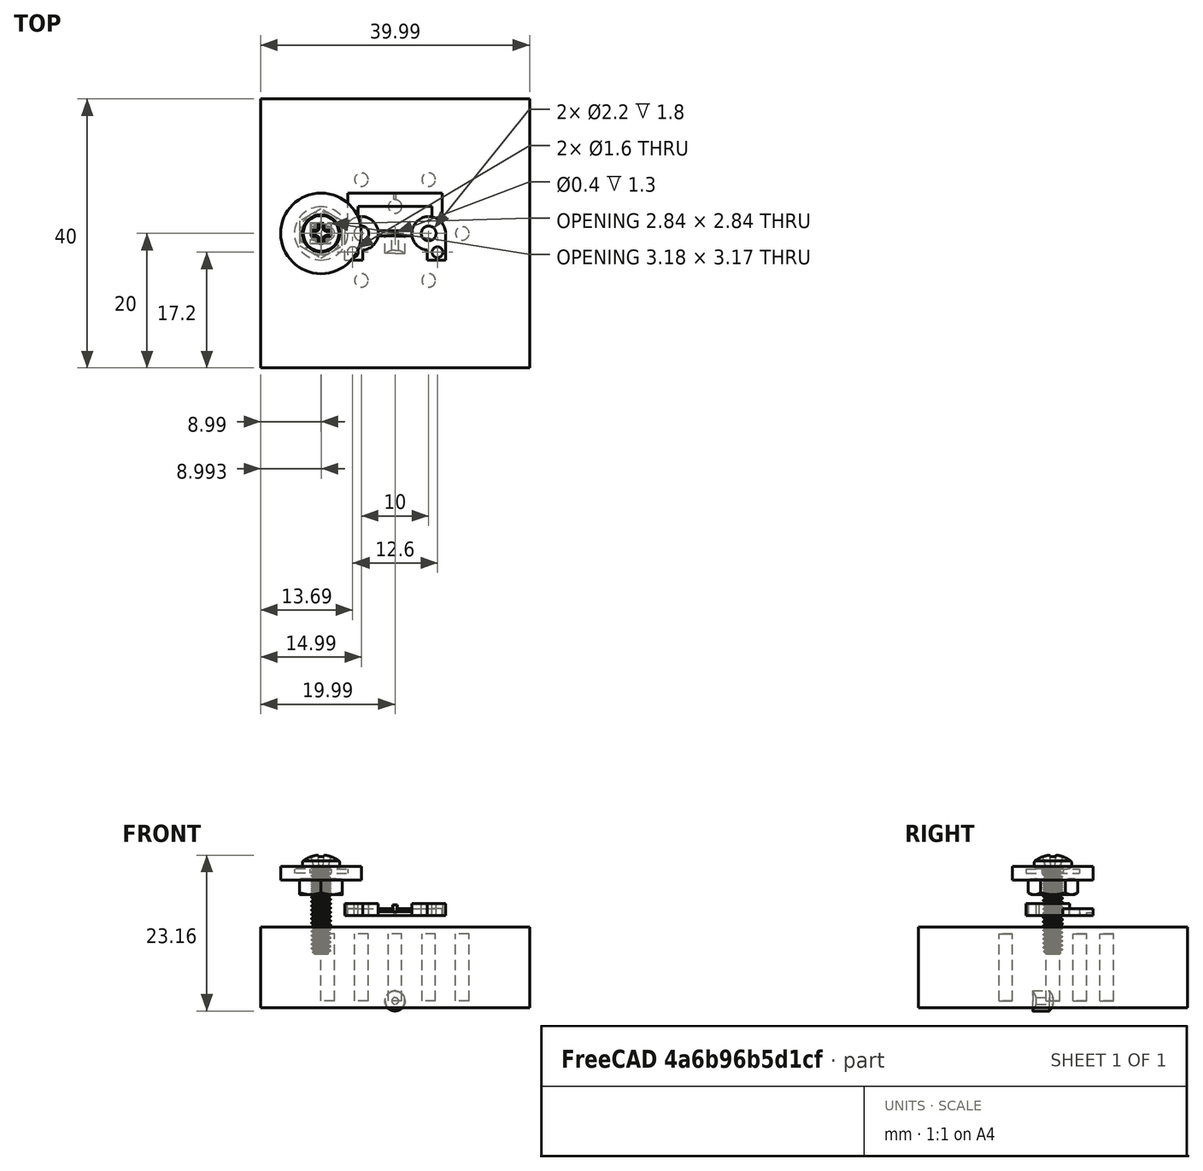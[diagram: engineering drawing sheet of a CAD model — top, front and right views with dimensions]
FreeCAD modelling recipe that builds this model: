
FCSTD DOCUMENT  (FreeCAD 0.18R16033 (Git))
Label: proto_baseplate
License: All rights reserved
LicenseURL: http://en.wikipedia.org/wiki/All_rights_reserved
objects: Part::Cylinder×13, Part::Feature×7, App::Part×4, Path::FeaturePython×4, Part::MultiFuse×3, Part::FeaturePython×2, Part::Cut×1, App::FeaturePython×1, App::DocumentObjectGroup×1, Path::FeatureCompoundPython×1
note: 27 computed .brp shape members not serialized (recipe doc carries the construction recipe); baked Part::Feature solids carry a one-line shape summary decoded from their .brp

FEATURE [Part::Cylinder] Cylinder  label="Baseplate"
  Angle = 360
  AttacherType = Attacher::AttachEngine3D
  Height = 10
  Radius = 19
FEATURE [Part::Cylinder] Cylinder001  label="Recess2"
  Angle = 360
  AttacherType = Attacher::AttachEngine3D
  Height = 1.5
  Placement = pos=(5,0,8.5) rot=(0,0,1;0rad)
  Radius = 1.7
FEATURE [Part::Cylinder] Cylinder002  label="Recess1"
  Angle = 360
  AttacherType = Attacher::AttachEngine3D
  Height = 1.5
  Placement = pos=(-5,0,8.5) rot=(0,0,1;0rad)
  Radius = 1.8
FEATURE [Part::MultiFuse] Fusion004
  Placement = pos=(0,0,13) rot=(0,0,1;0rad)
FEATURE [Part::Feature] Part__Feature  label="1"
  shape: bbox 5.8 x 3 x 3.036 mm, 8 faces (baked)
FEATURE [App::Part] CER_4  label="CER-4"
  Group = -> [Part__Feature]
  Origin = -> Origin
  Placement = pos=(-5,0,13) rot=(1,0,0;1.5708rad)
FEATURE [Part::Feature] Part__Feature001  label="1001"
  shape: bbox 5.8 x 3 x 3.036 mm, 8 faces (baked)
FEATURE [App::Part] CER_005  label="CER-005"
  Group = -> [Part__Feature001]
  Origin = -> Origin001
  Placement = pos=(5,0,13) rot=(1,0,0;1.5708rad)
FEATURE [Part::Feature] Part__Feature002  label="1001001"
  shape: bbox 5.8 x 3 x 3.036 mm, 8 faces (baked)
FEATURE [App::Part] CER_006  label="CER-006"
  Group = -> [Part__Feature002]
  Origin = -> Origin002
  Placement = pos=(5,0,17.5) rot=(1,0,0;1.5708rad)
FEATURE [Part::Feature] Part__Feature003  label="1001001001"
  shape: bbox 5.8 x 3 x 3.036 mm, 8 faces (baked)
FEATURE [App::Part] CER_007  label="CER-007"
  Group = -> [Part__Feature003]
  Origin = -> Origin003
  Placement = pos=(-5,0,17.5) rot=(1,0,0;1.5708rad)
FEATURE [Part::Cylinder] Cylinder003  label="ThreadedHole"
  Angle = 360
  AttacherType = Attacher::AttachEngine3D
  Height = 10
  Placement = pos=(-15,0,0) rot=(0,0,1;0rad)
  Radius = 1
FEATURE [Part::Feature] Part__Feature004  label="90107A005"
  Placement = pos=(-11,0,19) rot=(1,0,0;1.5708rad)
  shape: bbox 7.925 x 7.925 x 0.6096 mm, 6 faces (baked)
FEATURE [Part::Feature] Part__Feature005  label="91772A110"
  Placement = pos=(-11,0,7) rot=(0,0,1;0rad)
  shape: bbox 6.021 x 6.021 x 15.01 mm, 152 faces (baked)
FEATURE [Part::Feature] Part__Feature006  label="91841A005"
  Placement = pos=(-11,0,17) rot=(1,0,0;1.5708rad)
  shape: bbox 7.333 x 7.333 x 2.885 mm, 41 faces (baked)
FEATURE [Part::FeaturePython] Array  # Draft array (typed FeaturePython)
  Angle = 360
  ArrayType = 1
  Axis = (0,0,1)
  Base = -> Cylinder003
  Center = (0,0,0)
  Fuse = false
  IntervalAxis = (0,0,0)
  IntervalX = (1,0,0)
  IntervalY = (0,1,0)
  IntervalZ = (0,0,1)
  NumberPolar = 8
  NumberX = 2
  NumberY = 2
  NumberZ = 1
FEATURE [Part::Cylinder] Cylinder004  label="ThreadedHole001"
  Angle = 360
  AttacherType = Attacher::AttachEngine3D
  Height = 10
  Placement = pos=(0,-4,0) rot=(0,0,1;0rad)
  Radius = 1
FEATURE [Part::MultiFuse] Fusion
  Shapes = -> [Cylinder004,Array,Cylinder002,Cylinder001]
FEATURE [Part::Cut] Cut
  Base = -> Cylinder
  Tool = -> Fusion
FEATURE [App::FeaturePython] SetupSheet  # Path/CAM operation (typed FeaturePython)
  ClearanceHeightExpression = OpStockZMax+SetupSheet.ClearanceHeightOffset
  ClearanceHeightOffset = 5
  FinalDepthExpression = OpFinalDepth
  HorizRapid = 0
  SafeHeightExpression = OpStockZMax+SetupSheet.SafeHeightOffset
  SafeHeightOffset = 3
  StartDepthExpression = OpStartDepth
  StepDownExpression = OpToolDiameter
  VertRapid = 0
FEATURE [App::DocumentObjectGroup] Model
  Group = -> [Cut]
FEATURE [Path::FeaturePython] T3__063_End_Mill  label="T3: 063 End Mill"  # Path/CAM operation (typed FeaturePython)
  HorizFeed = 3
  HorizRapid = 0
  SpindleDir = 0
  SpindleSpeed = 24000
  ToolNumber = 1
  VertFeed = 2
  VertRapid = 0
  expr: HorizRapid = SetupSheet.HorizRapid
  expr: VertRapid = SetupSheet.VertRapid
FEATURE [Path::FeaturePython] Drilling  # Path/CAM operation (typed FeaturePython)
  Active = false
  AddTipLength = false
  ClearanceHeight = 16
  DwellEnabled = false
  DwellTime = 0
  FinalDepth = 8
  OpFinalDepth = 10
  OpStartDepth = 11
  OpStockZMax = 11
  OpStockZMin = -1
  OpToolDiameter = 1.58
  PeckDepth = 0
  PeckEnabled = false
  RetractHeight = 10
  ReturnLevel = 0
  SafeHeight = 14
  StartDepth = 11
  ToolController = -> T3__063_End_Mill
  expr: ClearanceHeight = OpStockZMax + SetupSheet.ClearanceHeightOffset
  expr: SafeHeight = OpStockZMax + SetupSheet.SafeHeightOffset
  expr: FinalDepth = 8
  expr: StartDepth = OpStartDepth
FEATURE [Path::FeaturePython] Pocket_Shape  # Path/CAM operation (typed FeaturePython)
  Active = true
  AreaParams:
    OpenMode = 0
    Angle = 45.0
    MinArcPoints = 4
    Coplanar = 0
    Tolerance = 1e-07
    CleanDistance = 0.0
    PocketExtraOffset = 0.0
    RoundPrecision = 0.0
    AngleShift = 0.0
    SubjectFill = 0
    PocketMode = 3
    PocketLastStepover = 0.0
    Simplify = False
    SectionTolerance = 1e-06
    MaxArcPoints = 100
    Offset = 0.0
    Accuracy = 0.01
    LastStepover = 0.0
    PocketStepover = 1.58
    ClipFill = 0
    ToolRadius = 0.79
    Outline = False
    ClipperScale = 10000000.0
    FromCenter = True
    Explode = False
    EndType = 0
    Shift = 0.0
    ExtraPass = 0
    Project = False
    JoinType = 0
    Thicken = False
    Stepdown = 1.0
    SectionMode = 2
    MiterLimit = 2.0
    Deflection = 0.01
    Reorient = True
    FitArcs = True
    SectionCount = -1
    SectionOffset = 0.0
    Stepover = 0.0
    Unit = 1.0
    Fill = 0
  Base = -> [Cut]
  ClearanceHeight = 16
  CutMode = 0
  ExtraOffset = 0
  FinalDepth = 8.5
  FinishDepth = 0
  KeepToolDown = false
  MinTravel = false
  OffsetPattern = 2
  OpFinalDepth = 8.5
  OpStartDepth = 11
  OpStockZMax = 11
  OpStockZMin = -1
  OpToolDiameter = 1.58
  PathParams = {'resume_height': 14.0, 'feedrate': 3.0, 'verbose': True, 'orientation': 1, 'return_end': True, 'preamble': False, 'retraction': 16.0, 'feedrate_v': 2.0}
  SafeHeight = 14
  StartAt = 0
  StartDepth = 11
  StartPoint = (0,0,0)
  StepDown = 0.5
  StepOver = 100
  ToolController = -> T3__063_End_Mill
  UseOutline = false
  UseStartPoint = false
  ZigZagAngle = 45
  expr: ClearanceHeight = OpStockZMax + SetupSheet.ClearanceHeightOffset
  expr: SafeHeight = OpStockZMax + SetupSheet.SafeHeightOffset
  expr: StepDown = 0.5
  expr: FinalDepth = OpFinalDepth
  expr: StartDepth = OpStartDepth
FEATURE [Path::FeatureCompoundPython] Operations  # Path/CAM operation (typed FeaturePython)
  Group = -> [Drilling,Pocket_Shape]
  UsePlacements = false
FEATURE [Part::Cylinder] Cylinder005  label="Cylinder"
  Angle = 360
  AttacherType = Attacher::AttachEngine3D
  Height = 2
  Placement = pos=(-11,0,18) rot=(0,0,1;0rad)
  Radius = 6
FEATURE [Part::Cylinder] Cylinder006  label="ThreadedHole002"
  Angle = 360
  AttacherType = Attacher::AttachEngine3D
  Height = 10
  Placement = pos=(-10,0,0) rot=(0,0,1;0rad)
  Radius = 1
FEATURE [Part::Cylinder] Cylinder007  label="ThreadedHole003"
  Angle = 360
  AttacherType = Attacher::AttachEngine3D
  Height = 10
  Placement = pos=(10,0,0) rot=(0,0,1;0rad)
  Radius = 1
FEATURE [Part::Cylinder] Cylinder008  label="ThreadedHole004"
  Angle = 360
  AttacherType = Attacher::AttachEngine3D
  Height = 10
  Placement = pos=(5,-7,0) rot=(0,0,1;0rad)
  Radius = 1
FEATURE [Part::Cylinder] Cylinder009  label="ThreadedHole005"
  Angle = 360
  AttacherType = Attacher::AttachEngine3D
  Height = 10
  Placement = pos=(-5,-7,0) rot=(0,0,1;0rad)
  Radius = 1
FEATURE [Part::Cylinder] Cylinder010  label="ThreadedHole006"
  Angle = 360
  AttacherType = Attacher::AttachEngine3D
  Height = 10
  Placement = pos=(-5,8,0) rot=(0,0,1;0rad)
  Radius = 1
FEATURE [Part::Cylinder] Cylinder011  label="ThreadedHole007"
  Angle = 360
  AttacherType = Attacher::AttachEngine3D
  Height = 10
  Placement = pos=(5,8,0) rot=(0,0,1;0rad)
  Radius = 1
FEATURE [Part::Cylinder] Cylinder012  label="ThreadedHole008"
  Angle = 360
  AttacherType = Attacher::AttachEngine3D
  Height = 10
  Placement = pos=(0,4,0) rot=(0,0,1;0rad)
  Radius = 1
FEATURE [Part::MultiFuse] Fusion005
  Shapes = -> [Cylinder012,Cylinder011,Cylinder010,Cylinder009,Cylinder008,Cylinder006,Cylinder007]
FEATURE [Part::FeaturePython] Stock  # WARN: FeaturePython — macro-defined, semantics opaque (R4)
  Base = -> Model
  ExtXneg = 1
  ExtXpos = 1
  ExtYneg = 1
  ExtYpos = 1
  ExtZneg = 1
  ExtZpos = 1
  Placement = pos=(-18.9857,-18.9964,0) rot=(0,0,1;0rad)
  StockType = FromBase
FEATURE [Path::FeaturePython] Job  # Path/CAM operation (typed FeaturePython)
  GeometryTolerance = 0.01
  Model = -> Model
  Operations = -> Operations
  PostProcessor = 7
  PostProcessorOutputFile = <userpath>/NAS/primary_a/Projects/ion_printer/files/ionprinter/mechanical/bowtie/gcode/baseplate_158.ngc
  SetupSheet = -> SetupSheet
  Stock = -> Stock
  ToolController = -> [T3__063_End_Mill]
